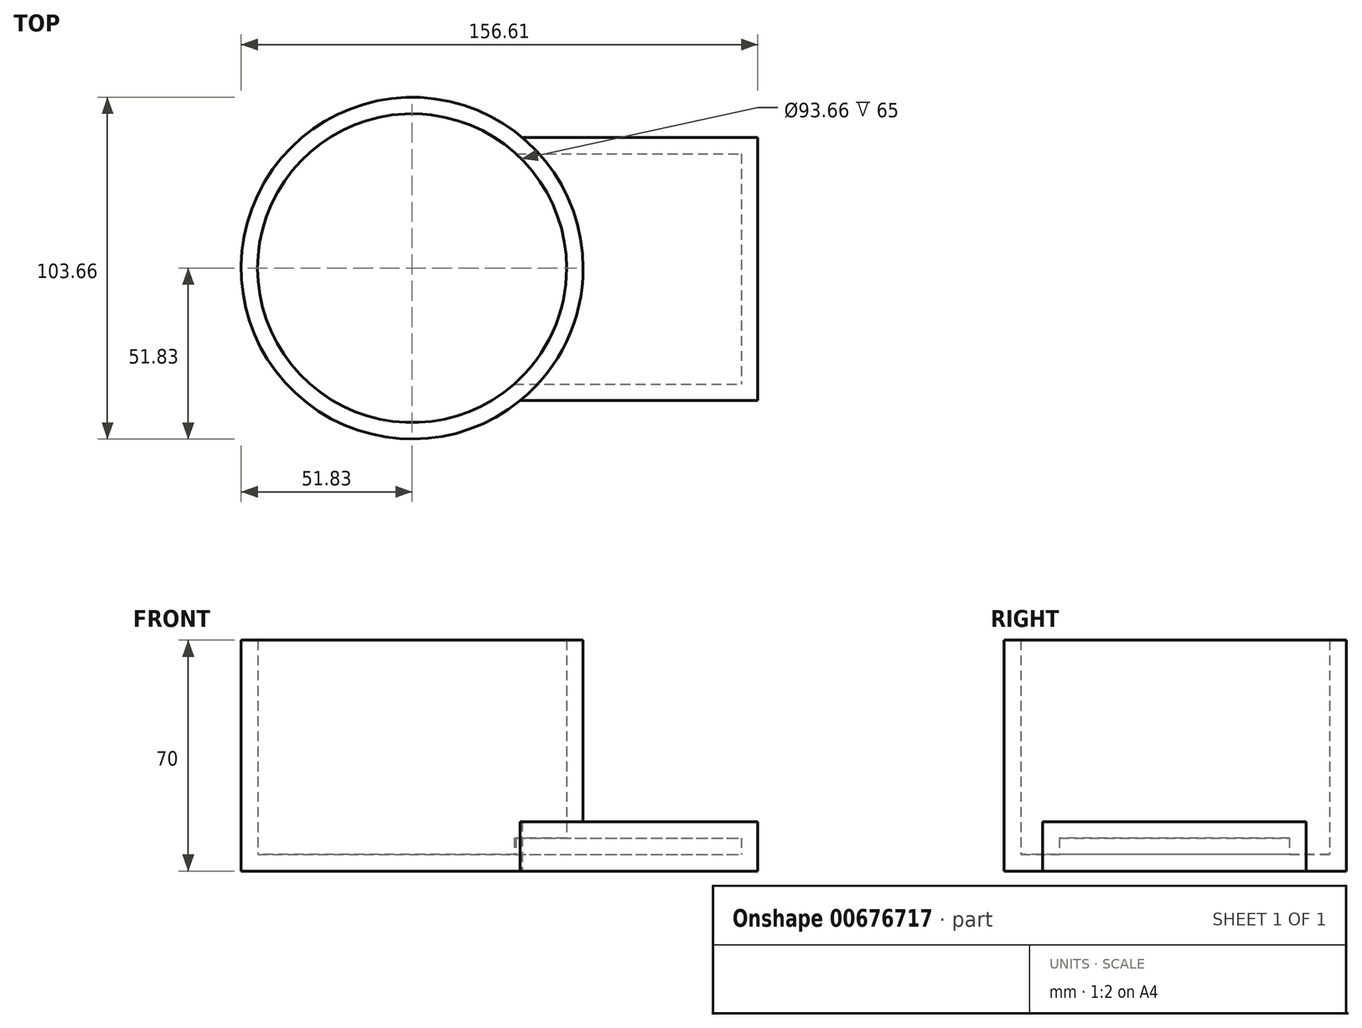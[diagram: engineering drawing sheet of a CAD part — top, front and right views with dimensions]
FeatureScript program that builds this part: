
annotation { "Feature Type Name" : "Feature", "Feature Type Description" : "" }
export const myFeature = defineFeature(function(context is Context, id is Id, definition is map)
    precondition{}
    {
        {
            var Q0;
            Q0=qCreatedBy(makeId("Top.planeOp"),FACE);
            var sketch = newSketch(context, id + "F0", { "sketchPlane" : qUnion([Q0])});
            skCircle(sketch, "E0", {"center": v(0, 0) * mm, "radius": 51.83 * mm});
            skSolve(sketch);
        }
        {
            var Q0;
            Q0=qCreatedBy(makeId("Top.planeOp"),FACE);
            var sketch = newSketch(context, id + "F1", { "sketchPlane" : qUnion([Q0])});
            skLineSegment(sketch, "E1.bottom", {"start": v(4.55, 39.68) * mm, "end": v(104.78, 39.68) * mm});
            skLineSegment(sketch, "E1.top", {"start": v(4.55, -40.15) * mm, "end": v(104.78, -40.15) * mm});
            skLineSegment(sketch, "E1.left", {"start": v(4.55, 39.68) * mm, "end": v(4.55, -40.15) * mm});
            skLineSegment(sketch, "E1.right", {"start": v(104.78, 39.68) * mm, "end": v(104.78, -40.15) * mm});
            skSolve(sketch);
        }
        {
            var Q0;
            Q0=makeQuery(id+"F0.imprint","IMPRINT",FACE,{"disambiguationData":[TD([[makeQuery(id+"F0.imprint","IMPRINT",EDGE,{"derivedFrom":sQuery(id+"F0.wireOp",EDGE,"E0")}),1.0]])]});
            extrude(context, id + "F2", {"entities" : qUnion([Q0]), "depth" : 70 * mm, "offsetDistance" : 25 * mm});
        }
        {
            var Q0;
            Q0=makeQuery(id+"F1.imprint","IMPRINT",FACE,{"disambiguationData":[TD([[makeQuery(id+"F1.imprint","IMPRINT",EDGE,{"derivedFrom":sQuery(id+"F1.wireOp",EDGE,"E1.bottom")}),-1.0]])]});
            extrude(context, id + "F3", {"entities" : qUnion([Q0]), "operationType" : NewBodyOperationType.ADD, "depth" : 15 * mm, "offsetDistance" : 25 * mm});
        }
        {
            var Q0;
            Q0=makeQuery(id+"F2.opExtrude","CAP_FACE",FACE,{"disambiguationData":[OSD([sQuery(id+"F0.wireOp",EDGE,"E0")])],"isStart":false});
            shell(context, id + "F4", {"entities" : qUnion([Q0]), "thickness" : 5 * mm});
        }
    });
